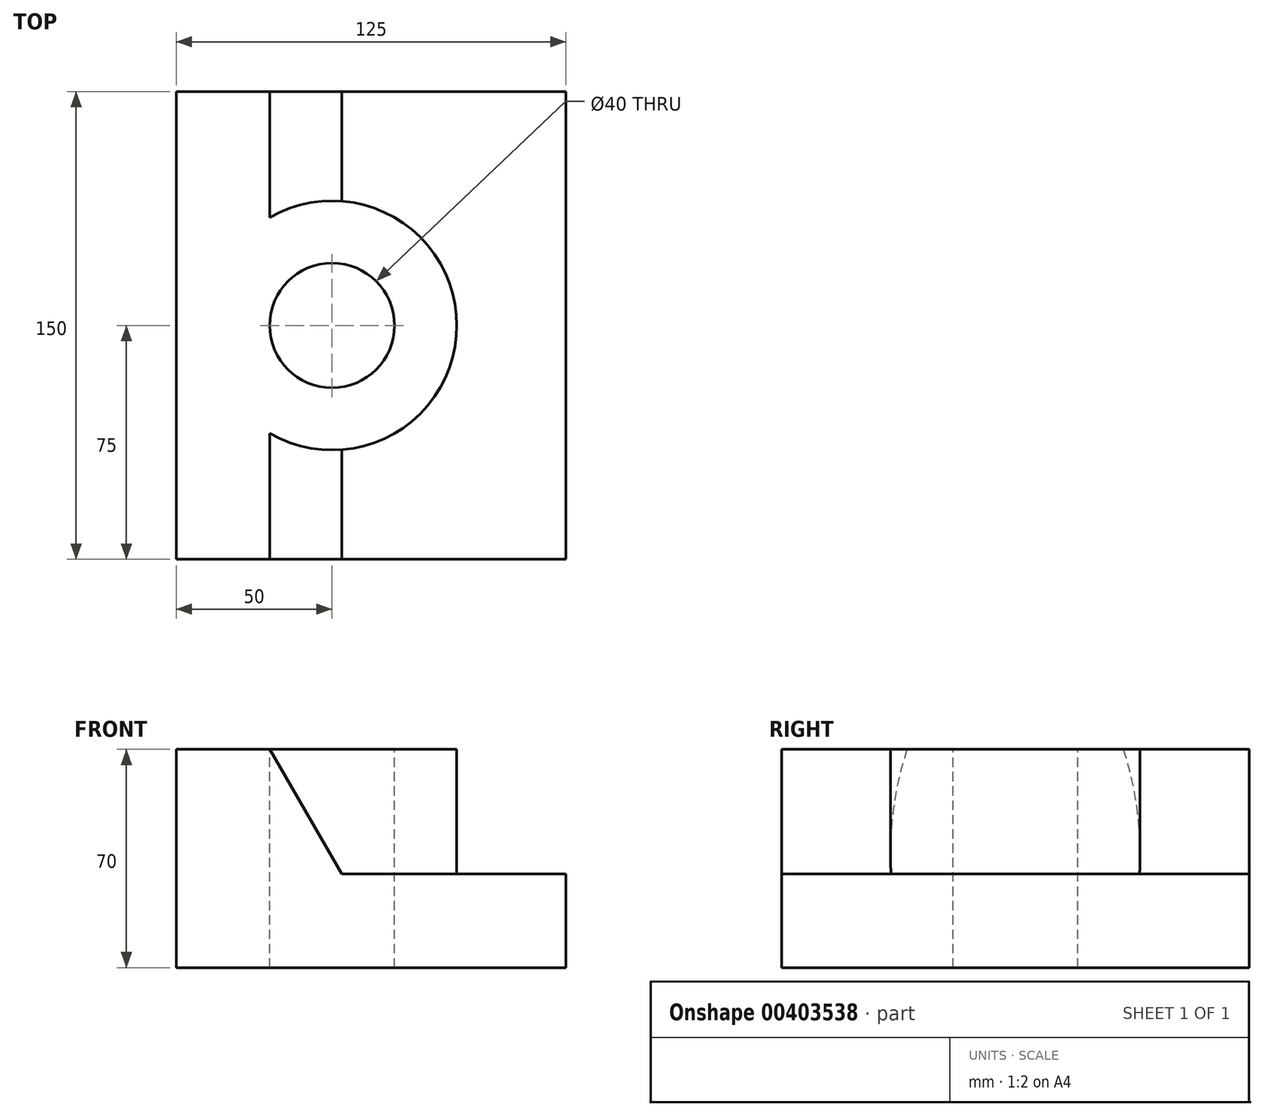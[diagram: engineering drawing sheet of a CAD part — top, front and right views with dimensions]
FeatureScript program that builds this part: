
annotation { "Feature Type Name" : "Feature", "Feature Type Description" : "" }
export const myFeature = defineFeature(function(context is Context, id is Id, definition is map)
    precondition{}
    {
        {
            var Q0;
            Q0=qCreatedBy(makeId("Front.planeOp"),FACE);
            var sketch = newSketch(context, id + "F0", { "sketchPlane" : qUnion([Q0])});
            skLineSegment(sketch, "E0", {"start": v(0, 0) * mm, "end": v(125, 0) * mm});
            skLineSegment(sketch, "E1", {"start": v(125, 0) * mm, "end": v(125, 30) * mm});
            skLineSegment(sketch, "E2", {"start": v(0, 0) * mm, "end": v(0, 70) * mm});
            skLineSegment(sketch, "E3", {"start": v(0, 70) * mm, "end": v(30, 70) * mm});
            skLineSegment(sketch, "E4", {"start": v(30, 70) * mm, "end": v(53.1, 30) * mm});
            skLineSegment(sketch, "E5", {"start": v(53.1, 30) * mm, "end": v(125, 30) * mm});
            skSolve(sketch);
        }
        {
            var Q0;
            Q0 = qSketchRegion(id + "F0", true);
            extrude(context, id + "F1", {"entities" : qUnion([Q0]), "oppositeDirection" : true, "depth" : 150 * mm});
        }
        {
            var Q0;
            Q0=makeQuery(id+"F1.opExtrude","SWEPT_FACE",FACE,{"disambiguationData":[OSD([sQuery(id+"F0.wireOp",EDGE,"E3")])]});
            var sketch = newSketch(context, id + "F2", { "sketchPlane" : qUnion([Q0])});
            skCircle(sketch, "E6", {"center": v(50, 75) * mm, "radius": 40 * mm});
            skSolve(sketch);
        }
        {
            var Q0;
            Q0 = qSketchRegion(id + "F2", true);
            var Q1;
            Q1=makeQuery(id+"F1.opExtrude","SWEPT_FACE",FACE,{"disambiguationData":[OSD([sQuery(id+"F0.wireOp",EDGE,"E5")])]});
            extrude(context, id + "F3", {"entities" : qUnion([Q0]), "operationType" : NewBodyOperationType.ADD, "endBound" : BoundingType.UP_TO_SURFACE, "oppositeDirection" : true, "endBoundEntityFace" : qUnion([Q1]), "depth" : 25 * mm});
        }
        {
            var Q0;
            Q0=makeQuery(id+"F3.boolean.opBoolean","MERGE",FACE,{"derivedFrom":[makeQuery(id+"F1.opExtrude","SWEPT_FACE",FACE,{"disambiguationData":[OSD([sQuery(id+"F0.wireOp",EDGE,"E3")])]}),makeQuery(id+"F3.opExtrude","CAP_FACE",FACE,{"disambiguationData":[OSD([sQuery(id+"F2.wireOp",EDGE,"E6")])],"isStart":true})]});
            var sketch = newSketch(context, id + "F4", { "sketchPlane" : qUnion([Q0])});
            skCircle(sketch, "E7", {"center": v(50, 75) * mm, "radius": 20 * mm});
            skSolve(sketch);
        }
        {
            var Q0;
            Q0 = qSketchRegion(id + "F4", true);
            extrude(context, id + "F5", {"entities" : qUnion([Q0]), "operationType" : NewBodyOperationType.REMOVE, "endBound" : BoundingType.THROUGH_ALL, "oppositeDirection" : true, "depth" : 25 * mm});
        }
    });
